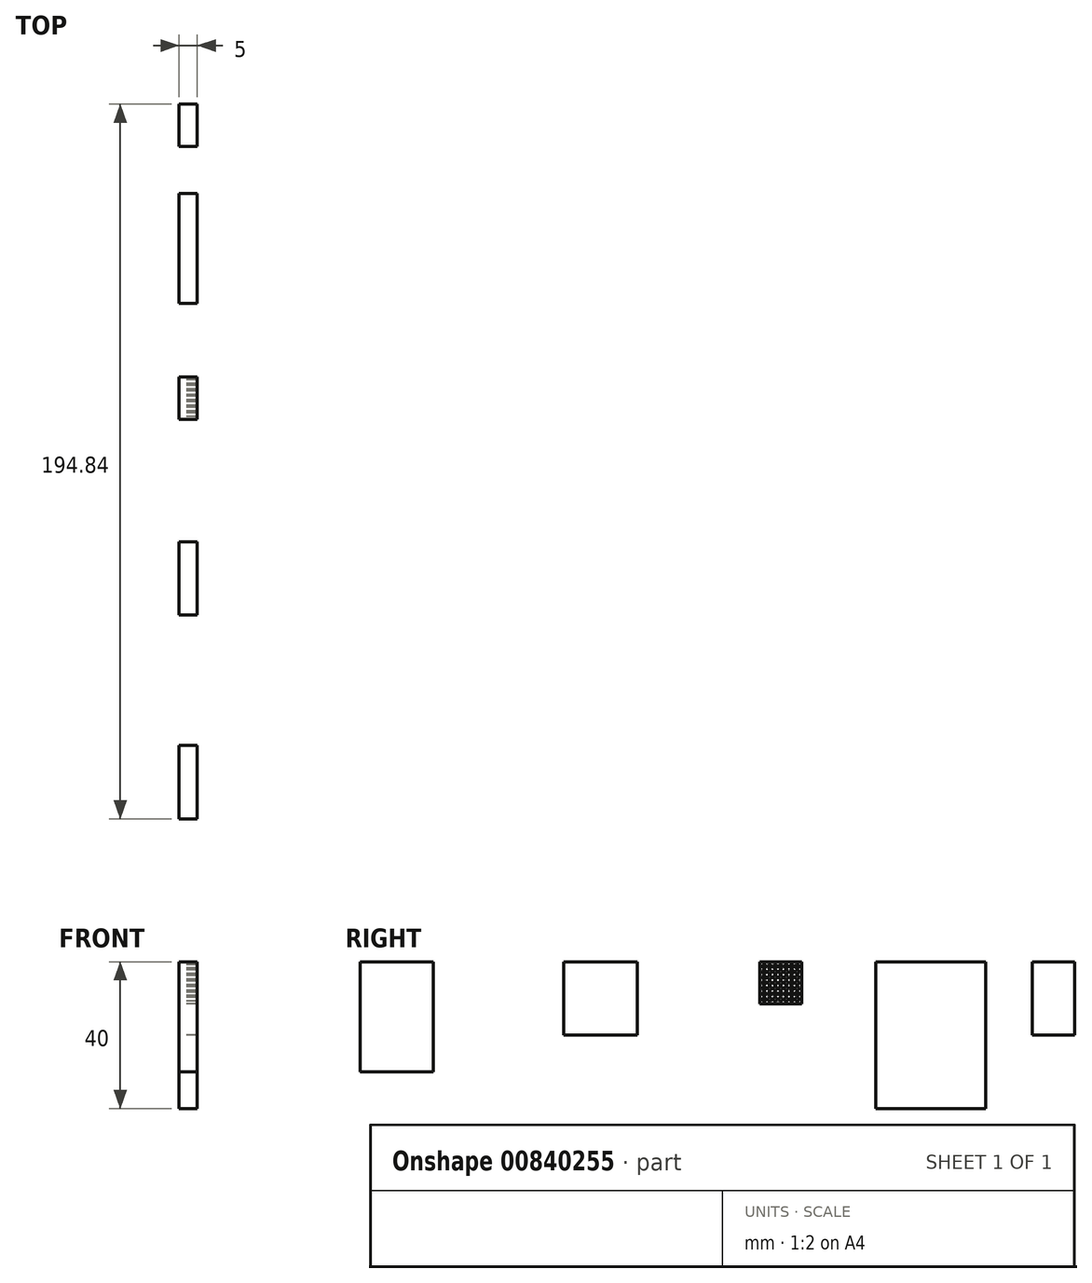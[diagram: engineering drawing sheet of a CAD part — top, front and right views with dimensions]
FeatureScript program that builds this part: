
annotation { "Feature Type Name" : "Feature", "Feature Type Description" : "" }
export const myFeature = defineFeature(function(context is Context, id is Id, definition is map)
    precondition{}
    {
        {
            var Q0;
            Q0=qCreatedBy(makeId("Right.planeOp"),FACE);
            var sketch = newSketch(context, id + "F0", { "sketchPlane" : qUnion([Q0])});
            skLineSegment(sketch, "E0.bottom", {"start": v(0, 0) * mm, "end": v(11.5, 0) * mm});
            skLineSegment(sketch, "E0.top", {"start": v(0, -11.5) * mm, "end": v(11.5, -11.5) * mm});
            skLineSegment(sketch, "E0.left", {"start": v(0, 0) * mm, "end": v(0, -11.5) * mm});
            skLineSegment(sketch, "E1.bottom", {"start": v(31.62, 0) * mm, "end": v(61.62, 0) * mm});
            skLineSegment(sketch, "E1.top", {"start": v(31.62, -40) * mm, "end": v(61.62, -40) * mm});
            skLineSegment(sketch, "E1.left", {"start": v(31.62, 0) * mm, "end": v(31.62, -40) * mm});
            skLineSegment(sketch, "E1.right", {"start": v(61.62, 0) * mm, "end": v(61.62, -40) * mm});
            skLineSegment(sketch, "E2.bottom", {"start": v(-53.4, 0) * mm, "end": v(-33.4, 0) * mm});
            skLineSegment(sketch, "E2.top", {"start": v(-53.4, -20) * mm, "end": v(-33.4, -20) * mm});
            skLineSegment(sketch, "E2.left", {"start": v(-53.4, 0) * mm, "end": v(-53.4, -20) * mm});
            skLineSegment(sketch, "E2.right", {"start": v(-33.4, 0) * mm, "end": v(-33.4, -20) * mm});
            skLineSegment(sketch, "E3.bottom", {"start": v(-88.95, 0) * mm, "end": v(-108.95, 0) * mm});
            skLineSegment(sketch, "E3.top", {"start": v(-88.95, -30) * mm, "end": v(-108.95, -30) * mm});
            skLineSegment(sketch, "E3.left", {"start": v(-88.95, 0) * mm, "end": v(-88.95, -30) * mm});
            skLineSegment(sketch, "E3.right", {"start": v(-108.95, 0) * mm, "end": v(-108.95, -30) * mm});
            skCircle(sketch, "E4", {"center": v(5.75, -5.75) * mm, "radius": 0.5 * mm});
            skLineSegment(sketch, "E5", {"start": v(11.5, 0) * mm, "end": v(11.5, -11.5) * mm});
            skCircle(sketch, "E6", {"center": v(5.75, -4.25) * mm, "radius": 0.5 * mm});
            skCircle(sketch, "E7", {"center": v(5.75, -2.75) * mm, "radius": 0.5 * mm});
            skCircle(sketch, "E8", {"center": v(4.25, -5.75) * mm, "radius": 0.5 * mm});
            skCircle(sketch, "E9", {"center": v(5.75, -1.25) * mm, "radius": 0.5 * mm});
            skCircle(sketch, "E10", {"center": v(4.25, -4.25) * mm, "radius": 0.5 * mm});
            skCircle(sketch, "E11", {"center": v(4.25, -2.75) * mm, "radius": 0.5 * mm});
            skCircle(sketch, "E12", {"center": v(4.25, -1.25) * mm, "radius": 0.5 * mm});
            skCircle(sketch, "E13", {"center": v(2.75, -5.75) * mm, "radius": 0.5 * mm});
            skCircle(sketch, "E14", {"center": v(2.75, -4.25) * mm, "radius": 0.5 * mm});
            skCircle(sketch, "E15", {"center": v(2.75, -2.75) * mm, "radius": 0.5 * mm});
            skCircle(sketch, "E16", {"center": v(2.75, -1.25) * mm, "radius": 0.5 * mm});
            skCircle(sketch, "E17", {"center": v(1.25, -5.75) * mm, "radius": 0.5 * mm});
            skCircle(sketch, "E18", {"center": v(1.25, -4.25) * mm, "radius": 0.5 * mm});
            skCircle(sketch, "E19", {"center": v(1.25, -2.75) * mm, "radius": 0.5 * mm});
            skCircle(sketch, "E20", {"center": v(1.25, -1.25) * mm, "radius": 0.5 * mm});
            skCircle(sketch, "E21.MirrorC", {"center": v(7.25, -1.25) * mm, "radius": 0.5 * mm});
            skCircle(sketch, "E22.MirrorC", {"center": v(7.25, -2.75) * mm, "radius": 0.5 * mm});
            skCircle(sketch, "E23.MirrorC", {"center": v(7.25, -4.25) * mm, "radius": 0.5 * mm});
            skCircle(sketch, "E24.MirrorC", {"center": v(7.25, -5.75) * mm, "radius": 0.5 * mm});
            skCircle(sketch, "E25.MirrorC", {"center": v(8.75, -5.75) * mm, "radius": 0.5 * mm});
            skCircle(sketch, "E26.MirrorC", {"center": v(8.75, -4.25) * mm, "radius": 0.5 * mm});
            skCircle(sketch, "E27.MirrorC", {"center": v(8.75, -2.75) * mm, "radius": 0.5 * mm});
            skCircle(sketch, "E28.MirrorC", {"center": v(8.75, -1.25) * mm, "radius": 0.5 * mm});
            skCircle(sketch, "E29.MirrorC", {"center": v(10.25, -1.25) * mm, "radius": 0.5 * mm});
            skCircle(sketch, "E30.MirrorC", {"center": v(10.25, -2.75) * mm, "radius": 0.5 * mm});
            skCircle(sketch, "E31.MirrorC", {"center": v(10.25, -4.25) * mm, "radius": 0.5 * mm});
            skCircle(sketch, "E32.MirrorC", {"center": v(10.25, -5.75) * mm, "radius": 0.5 * mm});
            skCircle(sketch, "E33.MirrorC", {"center": v(1.25, -7.25) * mm, "radius": 0.5 * mm});
            skCircle(sketch, "E34.MirrorC", {"center": v(2.75, -7.25) * mm, "radius": 0.5 * mm});
            skCircle(sketch, "E35.MirrorC", {"center": v(4.25, -7.25) * mm, "radius": 0.5 * mm});
            skCircle(sketch, "E36.MirrorC", {"center": v(4.25, -8.75) * mm, "radius": 0.5 * mm});
            skCircle(sketch, "E37.MirrorC", {"center": v(2.75, -8.75) * mm, "radius": 0.5 * mm});
            skCircle(sketch, "E38.MirrorC", {"center": v(1.25, -8.75) * mm, "radius": 0.5 * mm});
            skCircle(sketch, "E39.MirrorC", {"center": v(1.25, -10.25) * mm, "radius": 0.5 * mm});
            skCircle(sketch, "E40.MirrorC", {"center": v(2.75, -10.25) * mm, "radius": 0.5 * mm});
            skCircle(sketch, "E41.MirrorC", {"center": v(4.25, -10.25) * mm, "radius": 0.5 * mm});
            skCircle(sketch, "E42.MirrorC", {"center": v(5.75, -10.25) * mm, "radius": 0.5 * mm});
            skCircle(sketch, "E43.MirrorC", {"center": v(5.75, -8.75) * mm, "radius": 0.5 * mm});
            skCircle(sketch, "E44.MirrorC", {"center": v(5.75, -7.25) * mm, "radius": 0.5 * mm});
            skCircle(sketch, "E45.MirrorC", {"center": v(7.25, -7.25) * mm, "radius": 0.5 * mm});
            skCircle(sketch, "E46.MirrorC", {"center": v(7.25, -8.75) * mm, "radius": 0.5 * mm});
            skCircle(sketch, "E47.MirrorC", {"center": v(7.25, -10.25) * mm, "radius": 0.5 * mm});
            skCircle(sketch, "E48.MirrorC", {"center": v(8.75, -10.25) * mm, "radius": 0.5 * mm});
            skCircle(sketch, "E49.MirrorC", {"center": v(8.75, -8.75) * mm, "radius": 0.5 * mm});
            skCircle(sketch, "E50.MirrorC", {"center": v(8.75, -7.25) * mm, "radius": 0.5 * mm});
            skCircle(sketch, "E51.MirrorC", {"center": v(10.25, -7.25) * mm, "radius": 0.5 * mm});
            skCircle(sketch, "E52.MirrorC", {"center": v(10.25, -8.75) * mm, "radius": 0.5 * mm});
            skCircle(sketch, "E53.MirrorC", {"center": v(10.25, -10.25) * mm, "radius": 0.5 * mm});
            skLineSegment(sketch, "E54.bottom", {"start": v(74.4, 0) * mm, "end": v(85.9, 0) * mm});
            skLineSegment(sketch, "E54.top", {"start": v(74.4, -20) * mm, "end": v(85.9, -20) * mm});
            skLineSegment(sketch, "E54.left", {"start": v(74.4, 0) * mm, "end": v(74.4, -20) * mm});
            skLineSegment(sketch, "E54.right", {"start": v(85.9, 0) * mm, "end": v(85.9, -20) * mm});
            skSolve(sketch);
        }
        {
            var Q0;
            Q0=makeQuery(id+"F0.imprint","IMPRINT",FACE,{"disambiguationData":[TD([[makeQuery(id+"F0.imprint","IMPRINT",EDGE,{"derivedFrom":sQuery(id+"F0.wireOp",EDGE,"E0.bottom")}),-1.0]])]});
            var Q1;
            Q1=makeQuery(id+"F0.imprint","IMPRINT",FACE,{"disambiguationData":[TD([[makeQuery(id+"F0.imprint","IMPRINT",EDGE,{"derivedFrom":sQuery(id+"F0.wireOp",EDGE,"E1.bottom")}),-1.0]])]});
            var Q2;
            Q2=makeQuery(id+"F0.imprint","IMPRINT",FACE,{"disambiguationData":[TD([[makeQuery(id+"F0.imprint","IMPRINT",EDGE,{"derivedFrom":sQuery(id+"F0.wireOp",EDGE,"E3.bottom")}),1.0]])]});
            var Q3;
            Q3=makeQuery(id+"F0.imprint","IMPRINT",FACE,{"disambiguationData":[TD([[makeQuery(id+"F0.imprint","IMPRINT",EDGE,{"derivedFrom":sQuery(id+"F0.wireOp",EDGE,"E2.bottom")}),-1.0]])]});
            var Q4;
            Q4=makeQuery(id+"F0.imprint","IMPRINT",FACE,{"disambiguationData":[TD([[makeQuery(id+"F0.imprint","IMPRINT",EDGE,{"derivedFrom":sQuery(id+"F0.wireOp",EDGE,"E54.bottom")}),-1.0]])]});
            extrude(context, id + "F1", {"entities" : qUnion([Q0, Q1, Q2, Q3, Q4]), "depth" : 5 * mm, "offsetDistance" : 25 * mm});
        }
    });
